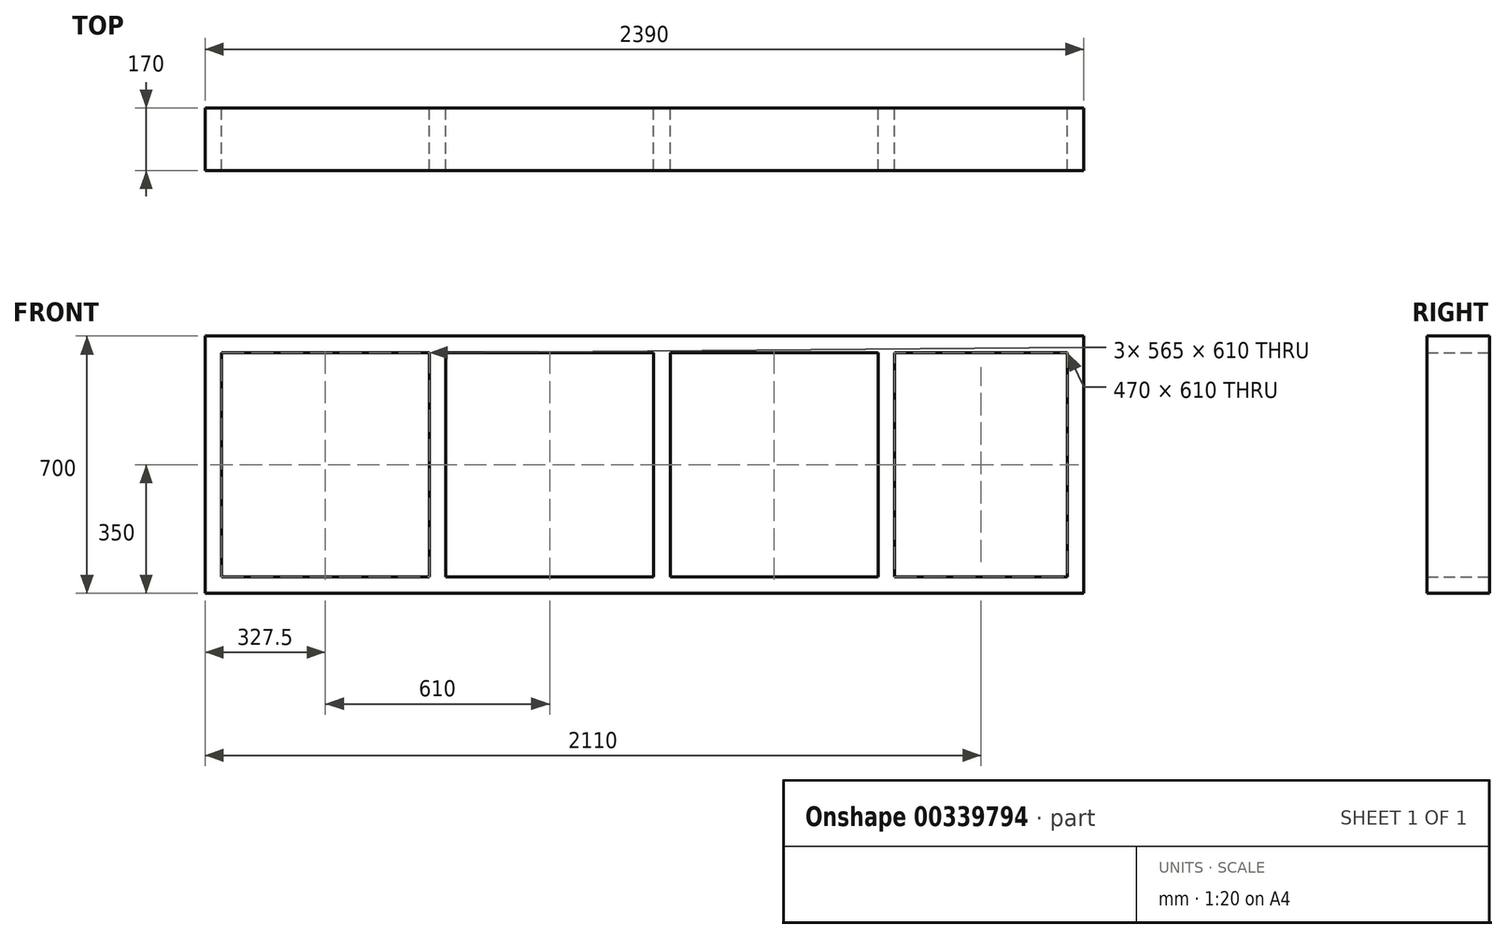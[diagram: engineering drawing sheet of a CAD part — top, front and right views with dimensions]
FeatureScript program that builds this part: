
annotation { "Feature Type Name" : "Feature", "Feature Type Description" : "" }
export const myFeature = defineFeature(function(context is Context, id is Id, definition is map)
    precondition{}
    {
        {
            var Q0;
            Q0=qCreatedBy(makeId("Front.planeOp"),FACE);
            var sketch = newSketch(context, id + "F0", { "sketchPlane" : qUnion([Q0])});
            skLineSegment(sketch, "E0.bottom", {"start": v(0, 0) * mm, "end": v(-2390, 0) * mm});
            skLineSegment(sketch, "E0.left", {"start": v(0, 0) * mm, "end": v(0, 700) * mm});
            skLineSegment(sketch, "E1.0", {"start": v(-2390, 45) * mm, "end": v(-2390, 700) * mm});
            skLineSegment(sketch, "E2.0", {"start": v(-1780, 45) * mm, "end": v(-1780, 655) * mm});
            skLineSegment(sketch, "E3.0", {"start": v(-1170, 45) * mm, "end": v(-1170, 655) * mm});
            skLineSegment(sketch, "E4.0", {"start": v(-560, 45) * mm, "end": v(-560, 655) * mm});
            skLineSegment(sketch, "E5.0", {"start": v(-2345, 45) * mm, "end": v(-2345, 655) * mm});
            skLineSegment(sketch, "E6.0", {"start": v(-1735, 45) * mm, "end": v(-1735, 655) * mm});
            skLineSegment(sketch, "E7.0", {"start": v(-1125, 45) * mm, "end": v(-1125, 655) * mm});
            skLineSegment(sketch, "E8.0", {"start": v(-515, 45) * mm, "end": v(-515, 655) * mm});
            skLineSegment(sketch, "E9.0", {"start": v(-45, 45) * mm, "end": v(-515, 45) * mm});
            skLineSegment(sketch, "E10.trimOffspring", {"start": v(-560, 45) * mm, "end": v(-1125, 45) * mm});
            skLineSegment(sketch, "E11.trimOffspring", {"start": v(-1170, 45) * mm, "end": v(-1735, 45) * mm});
            skLineSegment(sketch, "E12.trimOffspring", {"start": v(-1780, 45) * mm, "end": v(-2345, 45) * mm});
            skLineSegment(sketch, "E13.0", {"start": v(-45, 45) * mm, "end": v(-45, 655) * mm});
            skLineSegment(sketch, "E14", {"start": v(-2390, 45) * mm, "end": v(-2390, 0) * mm});
            skLineSegment(sketch, "E15", {"start": v(-2390, 0) * mm, "end": v(-2390, 700) * mm});
            skLineSegment(sketch, "E16", {"start": v(-2390, 700) * mm, "end": v(0, 700) * mm});
            skLineSegment(sketch, "E17.0", {"start": v(-2345, 655) * mm, "end": v(-1780, 655) * mm});
            skLineSegment(sketch, "E18.trimOffspring", {"start": v(-1735, 655) * mm, "end": v(-1170, 655) * mm});
            skLineSegment(sketch, "E19.trimOffspring", {"start": v(-1125, 655) * mm, "end": v(-560, 655) * mm});
            skLineSegment(sketch, "E20.trimOffspring", {"start": v(-515, 655) * mm, "end": v(-45, 655) * mm});
            skSolve(sketch);
        }
        {
            var Q0;
            Q0=makeQuery(id+"F0.imprint","IMPRINT",FACE,{"disambiguationData":[TD([[makeQuery(id+"F0.imprint","IMPRINT",EDGE,{"derivedFrom":sQuery(id+"F0.wireOp",EDGE,"E0.bottom")}),-1.0]])]});
            extrude(context, id + "F1", {"entities" : qUnion([Q0]), "depth" : 170 * mm});
        }
    });
